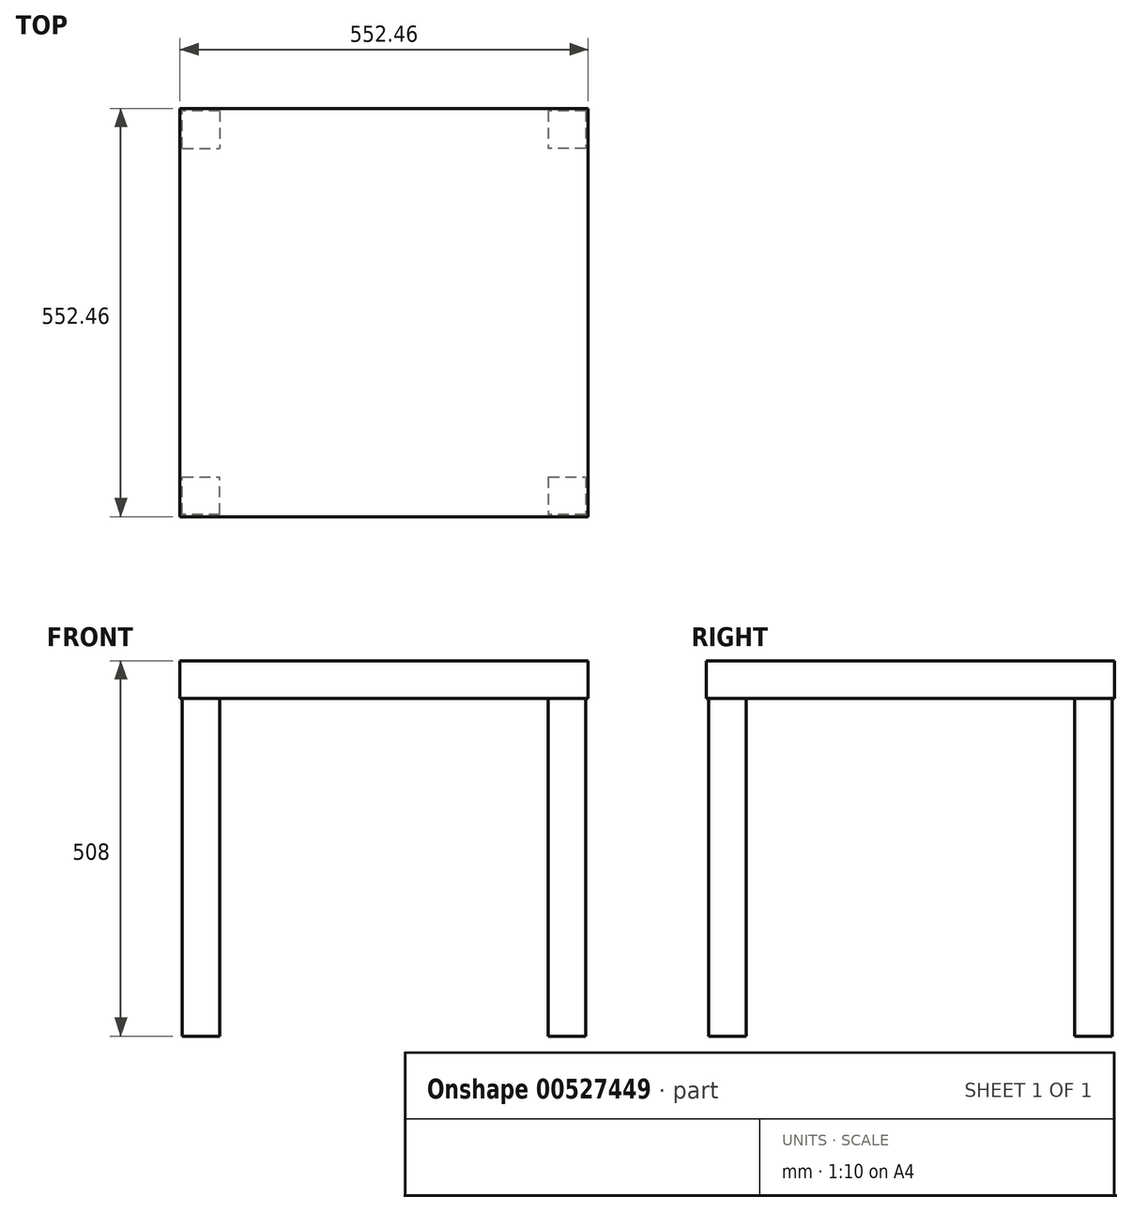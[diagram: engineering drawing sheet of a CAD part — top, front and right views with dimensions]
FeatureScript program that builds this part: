
annotation { "Feature Type Name" : "Feature", "Feature Type Description" : "" }
export const myFeature = defineFeature(function(context is Context, id is Id, definition is map)
    precondition{}
    {
        {
            var Q0;
            Q0=qCreatedBy(makeId("Top.planeOp"),FACE);
            var sketch = newSketch(context, id + "F0", { "sketchPlane" : qUnion([Q0])});
            skLineSegment(sketch, "E0.bottom", {"start": v(273.05, 273.05) * mm, "end": v(-273.05, 273.05) * mm});
            skLineSegment(sketch, "E0.top", {"start": v(273.05, -273.05) * mm, "end": v(-273.05, -273.05) * mm});
            skLineSegment(sketch, "E0.left", {"start": v(273.05, 273.05) * mm, "end": v(273.05, -273.05) * mm});
            skLineSegment(sketch, "E0.right", {"start": v(-273.05, 273.05) * mm, "end": v(-273.05, -273.05) * mm});
            skPoint(sketch, "E0.middle", {"position": v(0, 0) * mm});
            skSolve(sketch);
        }
        {
            var Q0;
            Q0=qCreatedBy(makeId("Top.planeOp"),FACE);
            var sketch = newSketch(context, id + "F1", { "sketchPlane" : qUnion([Q0])});
            skLineSegment(sketch, "E1.bottom", {"start": v(-273.05, 273.05) * mm, "end": v(-222.25, 273.05) * mm});
            skLineSegment(sketch, "E1.top", {"start": v(-273.05, 222.25) * mm, "end": v(-222.25, 222.25) * mm});
            skLineSegment(sketch, "E1.left", {"start": v(-273.05, 273.05) * mm, "end": v(-273.05, 222.25) * mm});
            skLineSegment(sketch, "E1.right", {"start": v(-222.25, 273.05) * mm, "end": v(-222.25, 222.25) * mm});
            skPoint(sketch, "E2.0", {"position": v(-273.05, 273.05) * mm});
            skSolve(sketch);
        }
        {
            var Q0;
            Q0=makeQuery(id+"F1.imprint","IMPRINT",FACE,{"disambiguationData":[TD([[makeQuery(id+"F1.imprint","IMPRINT",EDGE,{"derivedFrom":sQuery(id+"F1.wireOp",EDGE,"E1.bottom")}),-1.0]])]});
            extrude(context, id + "F2", {"entities" : qUnion([Q0]), "depth" : 508 * mm, "offsetDistance" : 25.4 * mm});
        }
        {
            var Q0;
            Q0=makeQuery(id+"F2.opExtrude","SWEPT_BODY",BODY,{"disambiguationData":[OSD([sQuery(id+"F1.wireOp",EDGE,"E1.bottom"),sQuery(id+"F1.wireOp",EDGE,"E1.top"),sQuery(id+"F1.wireOp",EDGE,"E1.left"),sQuery(id+"F1.wireOp",EDGE,"E1.right")])]});
            var Q1;
            Q1=qCreatedBy(makeId("Right.planeOp"),FACE);
            mirror(context, id + "F3", {"entities" : qUnion([Q0]), "mirrorPlane" : qUnion([Q1])});
        }
        {
            var Q0;
            Q0=makeQuery(id+"F2.opExtrude","SWEPT_BODY",BODY,{"disambiguationData":[OSD([sQuery(id+"F1.wireOp",EDGE,"E1.bottom"),sQuery(id+"F1.wireOp",EDGE,"E1.top"),sQuery(id+"F1.wireOp",EDGE,"E1.left"),sQuery(id+"F1.wireOp",EDGE,"E1.right")])]});
            var Q1;
            Q1=makeQuery(id+"F3.opPattern","COPY",BODY,{"derivedFrom":makeQuery(id+"F2.opExtrude","SWEPT_BODY",BODY,{"disambiguationData":[OSD([sQuery(id+"F1.wireOp",EDGE,"E1.bottom"),sQuery(id+"F1.wireOp",EDGE,"E1.top"),sQuery(id+"F1.wireOp",EDGE,"E1.left"),sQuery(id+"F1.wireOp",EDGE,"E1.right")])]}),"instanceName":"1"});
            var Q2;
            Q2=qCreatedBy(makeId("Front.planeOp"),FACE);
            mirror(context, id + "F4", {"entities" : qUnion([Q0, Q1]), "mirrorPlane" : qUnion([Q2])});
        }
        {
            var Q0;
            Q0=makeQuery(id+"F2.opExtrude","CAP_FACE",FACE,{"disambiguationData":[OSD([sQuery(id+"F1.wireOp",EDGE,"E1.bottom"),sQuery(id+"F1.wireOp",EDGE,"E1.top"),sQuery(id+"F1.wireOp",EDGE,"E1.left"),sQuery(id+"F1.wireOp",EDGE,"E1.right")])],"isStart":false});
            var sketch = newSketch(context, id + "F5", { "sketchPlane" : qUnion([Q0])});
            skLineSegment(sketch, "E3.0.0", {"start": v(-273.05, -273.05) * mm, "end": v(273.05, -273.05) * mm});
            skLineSegment(sketch, "E3.0.1", {"start": v(273.05, -273.05) * mm, "end": v(273.05, 273.05) * mm});
            skLineSegment(sketch, "E3.0.2", {"start": v(273.05, 273.05) * mm, "end": v(-273.05, 273.05) * mm});
            skLineSegment(sketch, "E3.0.3", {"start": v(-273.05, 273.05) * mm, "end": v(-273.05, -273.05) * mm});
            skSolve(sketch);
        }
        {
            var Q0;
            {var subQ2=sQuery(id+"F5.wireOp",EDGE,"E3.0.0");Q0=makeQuery(id+"F5.imprint","IMPRINT",FACE,{"disambiguationData":[TD([[makeQuery(id+"F5.imprint","IMPRINT",EDGE,{"derivedFrom":subQ2}),1.0]])]});}
            var Q1;
            {var subQ4=makeQuery(id+"F2.opExtrude","CAP_EDGE",EDGE,{"disambiguationData":[OSD([sQuery(id+"F1.wireOp",EDGE,"E1.top")])],"isStart":false});Q1=makeQuery(id+"F5.imprint","IMPRINT",FACE,{"disambiguationData":[TD([[makeQuery(id+"F5.imprint","IMPRINT",EDGE,{"derivedFrom":subQ4}),1.0]])]});}
            extrude(context, id + "F6", {"entities" : qUnion([Q0, Q1]), "oppositeDirection" : true, "depth" : 50.8 * mm, "offsetDistance" : 25.4 * mm});
        }
        {
            var Q0;
            Q0=makeQuery(id+"F2.opExtrude","SWEPT_BODY",BODY,{"disambiguationData":[OSD([sQuery(id+"F1.wireOp",EDGE,"E1.bottom"),sQuery(id+"F1.wireOp",EDGE,"E1.top"),sQuery(id+"F1.wireOp",EDGE,"E1.left"),sQuery(id+"F1.wireOp",EDGE,"E1.right")])]});
            var Q1;
            Q1=makeQuery(id+"F6.opExtrude","SWEPT_BODY",BODY,{"disambiguationData":[OSD([sQuery(id+"F5.wireOp",EDGE,"E3.0.0"),sQuery(id+"F5.wireOp",EDGE,"E3.0.1"),sQuery(id+"F5.wireOp",EDGE,"E3.0.2"),sQuery(id+"F5.wireOp",EDGE,"E3.0.3")])]});
            var Q2;
            Q2=makeQuery(id+"F3.opPattern","COPY",BODY,{"derivedFrom":makeQuery(id+"F2.opExtrude","SWEPT_BODY",BODY,{"disambiguationData":[OSD([sQuery(id+"F1.wireOp",EDGE,"E1.bottom"),sQuery(id+"F1.wireOp",EDGE,"E1.top"),sQuery(id+"F1.wireOp",EDGE,"E1.left"),sQuery(id+"F1.wireOp",EDGE,"E1.right")])]}),"instanceName":"1"});
            var Q3;
            Q3=makeQuery(id+"F4.opPattern","COPY",BODY,{"derivedFrom":makeQuery(id+"F2.opExtrude","SWEPT_BODY",BODY,{"disambiguationData":[OSD([sQuery(id+"F1.wireOp",EDGE,"E1.bottom"),sQuery(id+"F1.wireOp",EDGE,"E1.top"),sQuery(id+"F1.wireOp",EDGE,"E1.left"),sQuery(id+"F1.wireOp",EDGE,"E1.right")])]}),"instanceName":"1"});
            var Q4;
            Q4=makeQuery(id+"F4.opPattern","COPY",BODY,{"derivedFrom":makeQuery(id+"F3.opPattern","COPY",BODY,{"derivedFrom":makeQuery(id+"F2.opExtrude","SWEPT_BODY",BODY,{"disambiguationData":[OSD([sQuery(id+"F1.wireOp",EDGE,"E1.bottom"),sQuery(id+"F1.wireOp",EDGE,"E1.top"),sQuery(id+"F1.wireOp",EDGE,"E1.left"),sQuery(id+"F1.wireOp",EDGE,"E1.right")])]}),"instanceName":"1"}),"instanceName":"1"});
            booleanBodies(context, id + "F7", {"operationType" : BooleanOperationType.UNION, "tools" : qUnion([Q0, Q1, Q2, Q3, Q4])});
        }
        {
            var Q0;
            Q0=makeQuery(id+"F7.opBoolean","MERGE",FACE,{"derivedFrom":[makeQuery(id+"F2.opExtrude","CAP_FACE",FACE,{"disambiguationData":[OSD([sQuery(id+"F1.wireOp",EDGE,"E1.bottom"),sQuery(id+"F1.wireOp",EDGE,"E1.top"),sQuery(id+"F1.wireOp",EDGE,"E1.left"),sQuery(id+"F1.wireOp",EDGE,"E1.right")])],"isStart":false}),makeQuery(id+"F6.opExtrude","CAP_FACE",FACE,{"disambiguationData":[OSD([sQuery(id+"F5.wireOp",EDGE,"E3.0.0"),sQuery(id+"F5.wireOp",EDGE,"E3.0.1"),sQuery(id+"F5.wireOp",EDGE,"E3.0.2"),sQuery(id+"F5.wireOp",EDGE,"E3.0.3")])],"isStart":true})]});
            var sketch = newSketch(context, id + "F8", { "sketchPlane" : qUnion([Q0])});
            skLineSegment(sketch, "E4.0", {"start": v(-276.23, 276.23) * mm, "end": v(-276.23, -276.22) * mm});
            skLineSegment(sketch, "E4.1", {"start": v(276.22, 276.23) * mm, "end": v(-276.23, 276.23) * mm});
            skLineSegment(sketch, "E4.2", {"start": v(276.23, -276.23) * mm, "end": v(276.22, 276.22) * mm});
            skLineSegment(sketch, "E4.3", {"start": v(-276.23, -276.23) * mm, "end": v(276.23, -276.23) * mm});
            skSolve(sketch);
        }
        {
            var Q0;
            Q0=makeQuery(id+"F8.imprint","IMPRINT",FACE,{"disambiguationData":[TD([[makeQuery(id+"F8.imprint","IMPRINT",EDGE,{"derivedFrom":sQuery(id+"F8.wireOp",EDGE,"E4.0")}),1.0]])]});
            var Q1;
            Q1=makeQuery(id+"F6.opExtrude","CAP_FACE",FACE,{"disambiguationData":[OSD([sQuery(id+"F5.wireOp",EDGE,"E3.0.0"),sQuery(id+"F5.wireOp",EDGE,"E3.0.1"),sQuery(id+"F5.wireOp",EDGE,"E3.0.2"),sQuery(id+"F5.wireOp",EDGE,"E3.0.3")])],"isStart":false});
            extrude(context, id + "F9", {"entities" : qUnion([Q0]), "operationType" : NewBodyOperationType.ADD, "endBound" : BoundingType.UP_TO_SURFACE, "oppositeDirection" : true, "depth" : 25.4 * mm, "endBoundEntityFace" : qUnion([Q1]), "offsetDistance" : 25.4 * mm});
        }
    });
